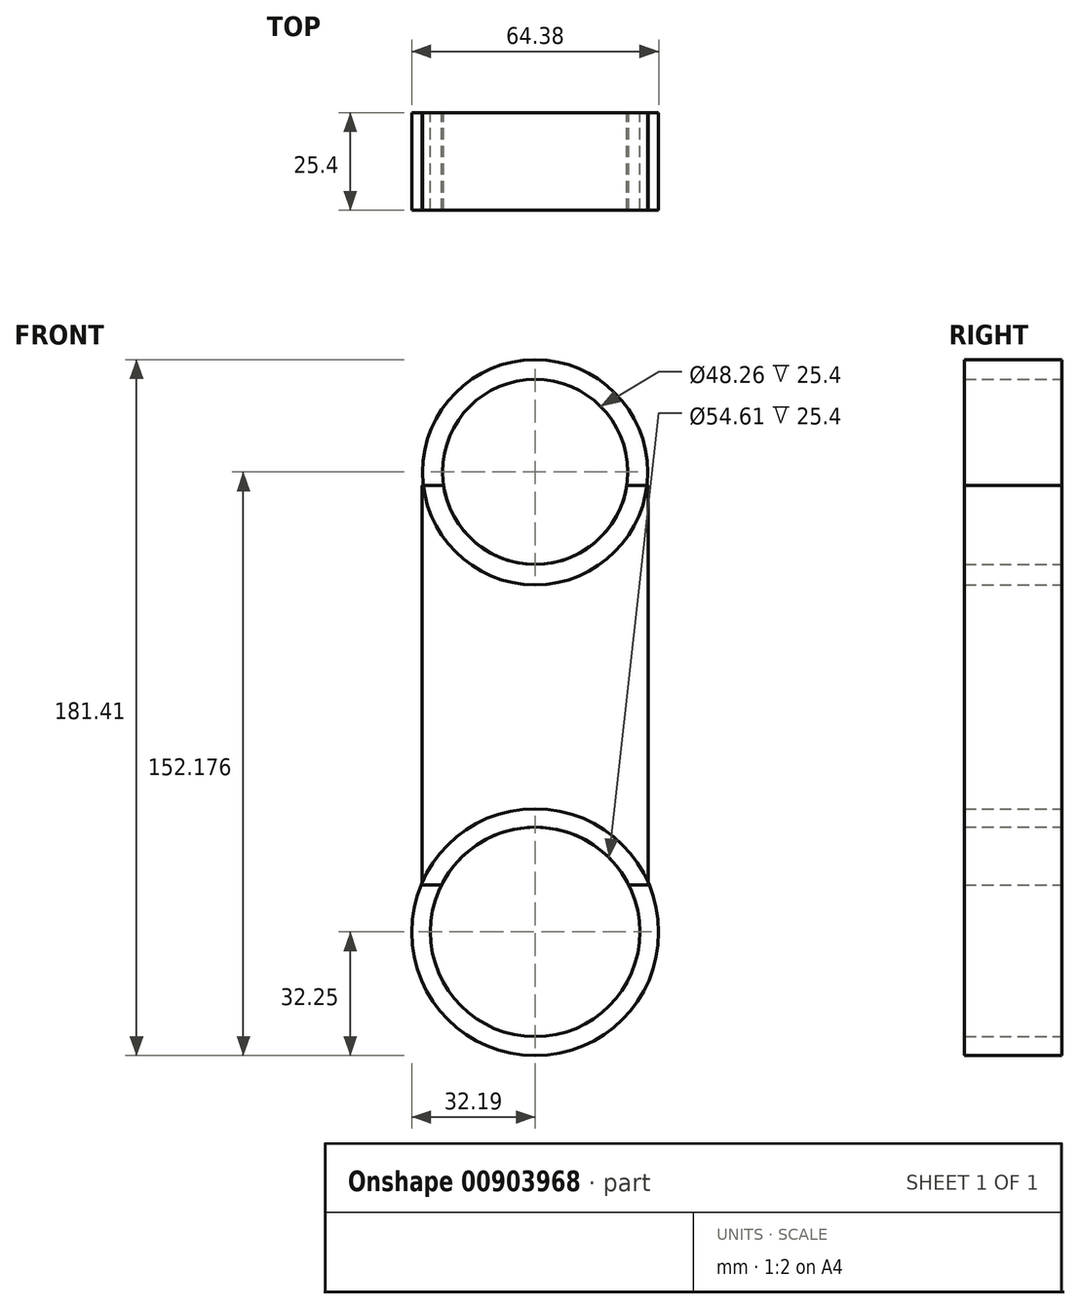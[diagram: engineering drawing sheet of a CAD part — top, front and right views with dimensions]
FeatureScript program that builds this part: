
annotation { "Feature Type Name" : "Feature", "Feature Type Description" : "" }
export const myFeature = defineFeature(function(context is Context, id is Id, definition is map)
    precondition{}
    {
        {
            var Q0;
            Q0=qCreatedBy(makeId("Front.planeOp"),FACE);
            var sketch = newSketch(context, id + "F0", { "sketchPlane" : qUnion([Q0])});
            skCircle(sketch, "E0", {"center": v(0, 45.54) * mm, "radius": 29.34 * mm});
            skCircle(sketch, "E1", {"center": v(0, -74.35) * mm, "radius": 32.19 * mm});
            skSolve(sketch);
        }
        {
            var Q0;
            Q0=qCreatedBy(makeId("Front.planeOp"),FACE);
            var sketch = newSketch(context, id + "F1", { "sketchPlane" : qUnion([Q0])});
            skLineSegment(sketch, "E2.bottom", {"start": v(-29.5, -62.08) * mm, "end": v(29.5, -62.08) * mm});
            skLineSegment(sketch, "E2.top", {"start": v(-29.5, 42.16) * mm, "end": v(29.5, 42.16) * mm});
            skLineSegment(sketch, "E2.left", {"start": v(-29.5, -62.08) * mm, "end": v(-29.5, 42.16) * mm});
            skLineSegment(sketch, "E2.right", {"start": v(29.5, -62.08) * mm, "end": v(29.5, 42.16) * mm});
            skPoint(sketch, "E2.middle", {"position": v(0, -9.96) * mm});
            skSolve(sketch);
        }
        {
            var Q0;
            Q0=qCreatedBy(makeId("Front.planeOp"),FACE);
            var sketch = newSketch(context, id + "F2", { "sketchPlane" : qUnion([Q0])});
            skCircle(sketch, "E3", {"center": v(0, 45.67) * mm, "radius": 24.16 * mm});
            skCircle(sketch, "E4", {"center": v(0, -74.29) * mm, "radius": 27.3 * mm});
            skSolve(sketch);
        }
        {
            var Q0;
            Q0=makeQuery(id+"F0.imprint","IMPRINT",FACE,{"disambiguationData":[TD([[makeQuery(id+"F0.imprint","IMPRINT",EDGE,{"derivedFrom":sQuery(id+"F0.wireOp",EDGE,"E0")}),1.0]])]});
            var Q1;
            Q1=makeQuery(id+"F0.imprint","IMPRINT",FACE,{"disambiguationData":[TD([[makeQuery(id+"F0.imprint","IMPRINT",EDGE,{"derivedFrom":sQuery(id+"F0.wireOp",EDGE,"E1")}),1.0]])]});
            var Q2;
            Q2=makeQuery(id+"F1.imprint","IMPRINT",FACE,{"disambiguationData":[TD([[makeQuery(id+"F1.imprint","IMPRINT",EDGE,{"derivedFrom":sQuery(id+"F1.wireOp",EDGE,"E2.bottom")}),1.0]])]});
            extrude(context, id + "F3", {"entities" : qUnion([Q0, Q1, Q2]), "depth" : 25.4 * mm, "offsetDistance" : 25.4 * mm});
        }
        {
            var Q0;
            Q0=qCreatedBy(makeId("Front.planeOp"),FACE);
            var sketch = newSketch(context, id + "F4", { "sketchPlane" : qUnion([Q0])});
            skCircle(sketch, "E5", {"center": v(0, 45.64) * mm, "radius": 24.15 * mm});
            skCircle(sketch, "E6", {"center": v(0, -74.27) * mm, "radius": 27.32 * mm});
            skSolve(sketch);
        }
        {
            var Q0;
            Q0=sQuery(id+"F2.wireOp",VERTEX,"E4.center");
            var Q1;
            Q1=makeQuery(id+"F3.opExtrude","SWEPT_BODY",BODY,{"disambiguationData":[OSD([sQuery(id+"F0.wireOp",EDGE,"E1")])]});
            var Q2;
            Q2=makeQuery(id+"F3.opExtrude","SWEPT_BODY",BODY,{"disambiguationData":[OSD([sQuery(id+"F1.wireOp",EDGE,"E2.bottom"),sQuery(id+"F1.wireOp",EDGE,"E2.top"),sQuery(id+"F1.wireOp",EDGE,"E2.left"),sQuery(id+"F1.wireOp",EDGE,"E2.right")])]});
            hole(context, id + "F5", {"style" : HoleStyle.SIMPLE, "endStyle" : HoleEndStyle.THROUGH, "oppositeDirection" : true, "holeDiameter" : 54.6 * mm, "majorDiameter" : 6.35 * mm, "isTappedThrough" : true, "tappedDepth" : 12.7 * mm, "tapClearance" : 3, "locations" : qUnion([Q0]), "scope" : qUnion([Q1, Q2])});
        }
        {
            var Q0;
            Q0=sQuery(id+"F4.wireOp",VERTEX,"E5.center");
            var Q1;
            Q1=makeQuery(id+"F3.opExtrude","SWEPT_BODY",BODY,{"disambiguationData":[OSD([sQuery(id+"F1.wireOp",EDGE,"E2.bottom"),sQuery(id+"F1.wireOp",EDGE,"E2.top"),sQuery(id+"F1.wireOp",EDGE,"E2.left"),sQuery(id+"F1.wireOp",EDGE,"E2.right")])]});
            var Q2;
            Q2=makeQuery(id+"F3.opExtrude","SWEPT_BODY",BODY,{"disambiguationData":[OSD([sQuery(id+"F0.wireOp",EDGE,"E0")])]});
            hole(context, id + "F6", {"style" : HoleStyle.SIMPLE, "endStyle" : HoleEndStyle.THROUGH, "oppositeDirection" : true, "holeDiameter" : 48.26 * mm, "majorDiameter" : 6.35 * mm, "isTappedThrough" : true, "tappedDepth" : 12.7 * mm, "tapClearance" : 3, "locations" : qUnion([Q0]), "scope" : qUnion([Q1, Q2])});
        }
    });
